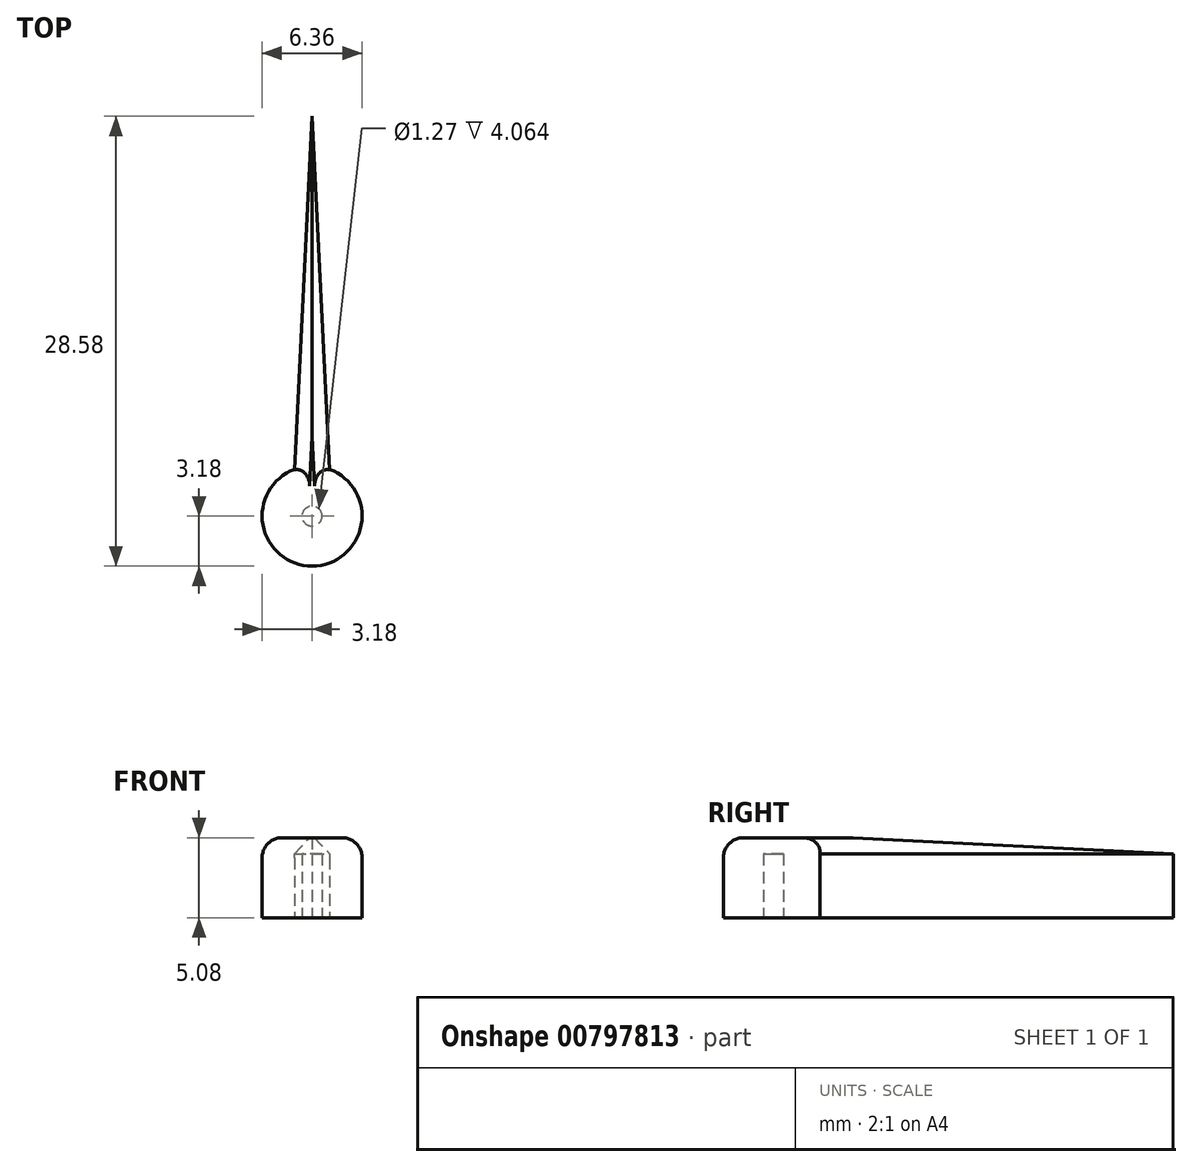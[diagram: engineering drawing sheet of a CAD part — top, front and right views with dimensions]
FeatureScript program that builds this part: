
annotation { "Feature Type Name" : "Feature", "Feature Type Description" : "" }
export const myFeature = defineFeature(function(context is Context, id is Id, definition is map)
    precondition{}
    {
        {
            var Q0;
            Q0=qCreatedBy(makeId("Top.planeOp"),FACE);
            var sketch = newSketch(context, id + "F0", { "sketchPlane" : qUnion([Q0])});
            skLineSegment(sketch, "E0", {"start": v(-1.27, 0) * mm, "end": v(0, 25.4) * mm});
            skLineSegment(sketch, "E1", {"start": v(0, 25.4) * mm, "end": v(1.27, 0) * mm});
            skLineSegment(sketch, "E2", {"start": v(0, 0) * mm, "end": v(-1.27, 0) * mm});
            skLineSegment(sketch, "E3", {"start": v(0, 0) * mm, "end": v(1.27, 0) * mm});
            skCircle(sketch, "E4", {"center": v(0, 0) * mm, "radius": 3.18 * mm});
            skSolve(sketch);
        }
        {
            var Q0;
            Q0 = qSketchRegion(id + "F0", true);
            var Q1;
            {var subQ0=sQuery(id+"F0.wireOp",EDGE,"E3");var subQ1=sQuery(id+"F0.wireOp",EDGE,"E2");var subQ2=makeQuery(id+"F0.imprint","INTERSECT",VERTEX,{"derivedFrom":[subQ1,subQ0]});Q1=makeQuery(id+"F0.imprint","IMPRINT",FACE,{"disambiguationData":[TD([[makeQuery(id+"F0.imprint","IMPRINT",EDGE,{"disambiguationData":[TD([[subQ2,-1.0]])],"derivedFrom":subQ1}),-1.0]])]});}
            var Q2;
            {var subQ0=sQuery(id+"F0.wireOp",EDGE,"E3");var subQ1=sQuery(id+"F0.wireOp",EDGE,"E2");var subQ2=makeQuery(id+"F0.imprint","INTERSECT",VERTEX,{"derivedFrom":[subQ1,subQ0]});Q2=makeQuery(id+"F0.imprint","IMPRINT",FACE,{"disambiguationData":[TD([[makeQuery(id+"F0.imprint","IMPRINT",EDGE,{"disambiguationData":[TD([[subQ2,-1.0]])],"derivedFrom":subQ1}),1.0]])]});}
            extrude(context, id + "F1", {"entities" : qUnion([Q0, Q1, Q2]), "depth" : 5.08 * mm, "offsetDistance" : 25.4 * mm});
        }
        {
            var Q0;
            Q0=makeQuery(id+"F1.opExtrude","CAP_EDGE",EDGE,{"disambiguationData":[OSD([sQuery(id+"F0.wireOp",EDGE,"E0")])],"isStart":false});
            var Q1;
            Q1=makeQuery(id+"F1.opExtrude","CAP_EDGE",EDGE,{"disambiguationData":[OSD([sQuery(id+"F0.wireOp",EDGE,"E1")])],"isStart":false});
            chamfer(context, id + "F2", {"entities" : qUnion([Q0, Q1]), "width" : 1.02 * mm, "tangentPropagation" : true});
        }
        {
            var Q0;
            Q0=makeQuery(id+"F1.opExtrude","CAP_EDGE",EDGE,{"disambiguationData":[OSD([sQuery(id+"F0.wireOp",EDGE,"E4")])],"isStart":false});
            fillet(context, id + "F3", {"entities" : qUnion([Q0]), "radius" : 1.27 * mm, "tangentPropagation" : true, "allowEdgeOverflow" : false});
        }
        {
            var Q0;
            Q0=qCreatedBy(makeId("Top.planeOp"),FACE);
            var sketch = newSketch(context, id + "F4", { "sketchPlane" : qUnion([Q0])});
            skCircle(sketch, "E5", {"center": v(0, 0) * mm, "radius": 0.64 * mm});
            skSolve(sketch);
        }
        {
            var Q0;
            Q0 = qSketchRegion(id + "F4", true);
            extrude(context, id + "F5", {"entities" : qUnion([Q0]), "operationType" : NewBodyOperationType.REMOVE, "depth" : 4.06 * mm, "offsetDistance" : 25.4 * mm});
        }
    });
